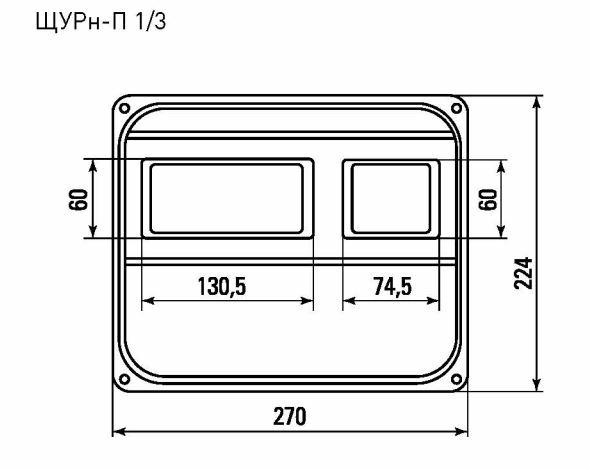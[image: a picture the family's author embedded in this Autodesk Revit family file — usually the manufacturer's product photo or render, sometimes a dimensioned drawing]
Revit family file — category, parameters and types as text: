
# Revit family: EKF_EE_ЩМП_IP31_Basic
name_source: partatom
category: Электрооборудование
units: mm (PartAtom-declared; Revit-internal decimal feet)

## family parameters
Всегда вертикально = Да
На основе рабочей плоскости = Нет
Общий = Нет
При загрузке вырезать с полостями = Нет
Размер круглого соединителя = Использовать диаметр
Тип детали = Силовой щит
Точка расчета площади = Да

## types (6) — shared parameters
ADSK_Единица измерения = компл.
ADSK_Завод-изготовитель = EKF
ADSK_Классификация нагрузок = Прочее
ADSK_Количество = 1
ADSK_Количество фаз = 3
ADSK_Коэффициент мощности = 1
ADSK_Материал = RAL 7035_Сталь
ADSK_Напряжение = 400 В
ADSK_Номинальная мощность = 0 Вт
ADSK_Полная мощность = 0 В·А
ADSK_Ток = 125 А
Изготовитель = EKF
Серия номенклатуры = Basic
Степень защиты IP = IP31
ТВ = EKF
Тип установки = Навесной
zero-valued in all types: ADSK_Масса, Количество DIN-реек, Количество модулей на DIN-рейке, Максимальное количество модулей

## per-type parameters (varying)
| type | ADSK_Код изделия | ADSK_Марка | ADSK_Наименование | ADSK_Обозначение | ADSK_Размер_Высота | ADSK_Размер_Глубина | ADSK_Размер_Ширина | Описание | Тип |
| ЩМП-27.21.14 (ЩМП-00) IP31 EKF Basic | mb22-00-bas | ЩМП-27.21.14 (ЩМП-00) IP31 | Щит с монтажной панелью ЩМП-27.21.14 (ЩМП-00) IP31 EKF Basic | ЩМП-27.21.14 (ЩМП-00) IP31 | 270 мм | 140 мм | 210 мм | Щит с монтажной панелью ЩМП-27.21.14 (ЩМП-00) IP31 EKF Basic | 82 мм |
| ЩМП-35.30.15 (ЩМП-03) IP31 EKF Basic | mb22-03-bas | ЩМП-35.30.15 (ЩМП-03) IP31 | Щит с монтажной панелью ЩМП-35.30.15 (ЩМП-03) IP31 EKF Basic | ЩМП-35.30.15 (ЩМП-03) IP31 | 350 мм | 150 мм | 300 мм | Щит с монтажной панелью ЩМП-35.30.15 (ЩМП-03) IP31 EKF Basic | 83 мм |
| ЩМП-40.30.15 (ЩМП-04) IP31 EKF Basic | mb22-04-bas | ЩМП-40.30.15 (ЩМП-04) IP31 | Щит с монтажной панелью ЩМП-40.30.15 (ЩМП-04) IP31 EKF Basic | ЩМП-40.30.15 (ЩМП-04) IP31 | 400 мм | 150 мм | 300 мм | Щит с монтажной панелью ЩМП-40.30.15 (ЩМП-04) IP31 EKF Basic | 84 мм |
| ЩМП-40.30.22 (ЩРНМ-1) IP31 EKF Basic | mb22-1-bas | ЩМП-40.30.22 (ЩРНМ-1) IP31 | Щит с монтажной панелью ЩМП-40.30.22 (ЩРНМ-1) IP31 EKF Basic | ЩМП-40.30.22 (ЩРНМ-1) IP31 | 400 мм | 220 мм | 300 мм | Щит с монтажной панелью ЩМП-40.30.22 (ЩРНМ-1) IP31 EKF Basic | 85 мм |
| ЩМП-50.40.22 (ЩРНМ-2) IP31 EKF Basic | mb22-2-bas | ЩМП-50.40.22 (ЩРНМ-2) IP31 | Щит с монтажной панелью ЩМП-50.40.22 (ЩРНМ-2) IP31 EKF Basic | ЩМП-50.40.22 (ЩРНМ-2) IP31 | 500 мм | 220 мм | 400 мм | Щит с монтажной панелью ЩМП-50.40.22 (ЩРНМ-2) IP31 EKF Basic | 86 мм |
| ЩМП-65.50.22 (ЩРНМ-3) IP31 EKF Basic | mb22-3-bas | ЩМП-65.50.22 (ЩРНМ-3) IP31 | Щит с монтажной панелью ЩМП-65.50.22 (ЩРНМ-3) IP31 EKF Basic | ЩМП-65.50.22 (ЩРНМ-3) IP31 | 650 мм | 220 мм | 500 мм | Щит с монтажной панелью ЩМП-65.50.22 (ЩРНМ-3) IP31 EKF Basic | 87 мм |
